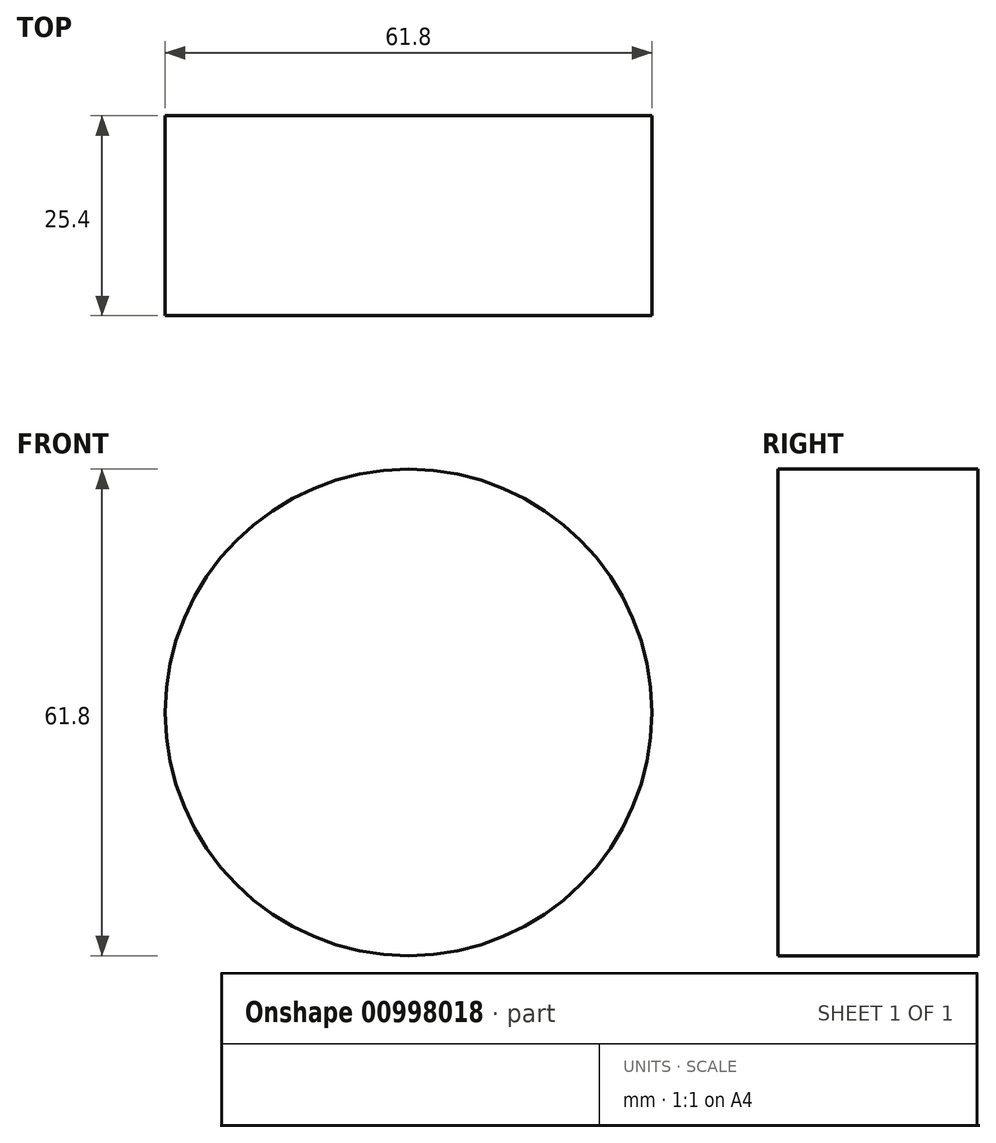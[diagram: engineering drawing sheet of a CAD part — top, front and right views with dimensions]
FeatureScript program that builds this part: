
annotation { "Feature Type Name" : "Feature", "Feature Type Description" : "" }
export const myFeature = defineFeature(function(context is Context, id is Id, definition is map)
    precondition{}
    {
        {
            var Q0;
            Q0=qCreatedBy(makeId("Front.planeOp"),FACE);
            var sketch = newSketch(context, id + "F0", { "sketchPlane" : qUnion([Q0])});
            skCircle(sketch, "E0", {"center": v(0, 0) * mm, "radius": 30.9 * mm});
            skSolve(sketch);
        }
        {
            var Q0;
            Q0 = qSketchRegion(id + "F0", true);
            extrude(context, id + "F1", {"entities" : qUnion([Q0]), "depth" : 25.4 * mm, "offsetDistance" : 25.4 * mm});
        }
    });
